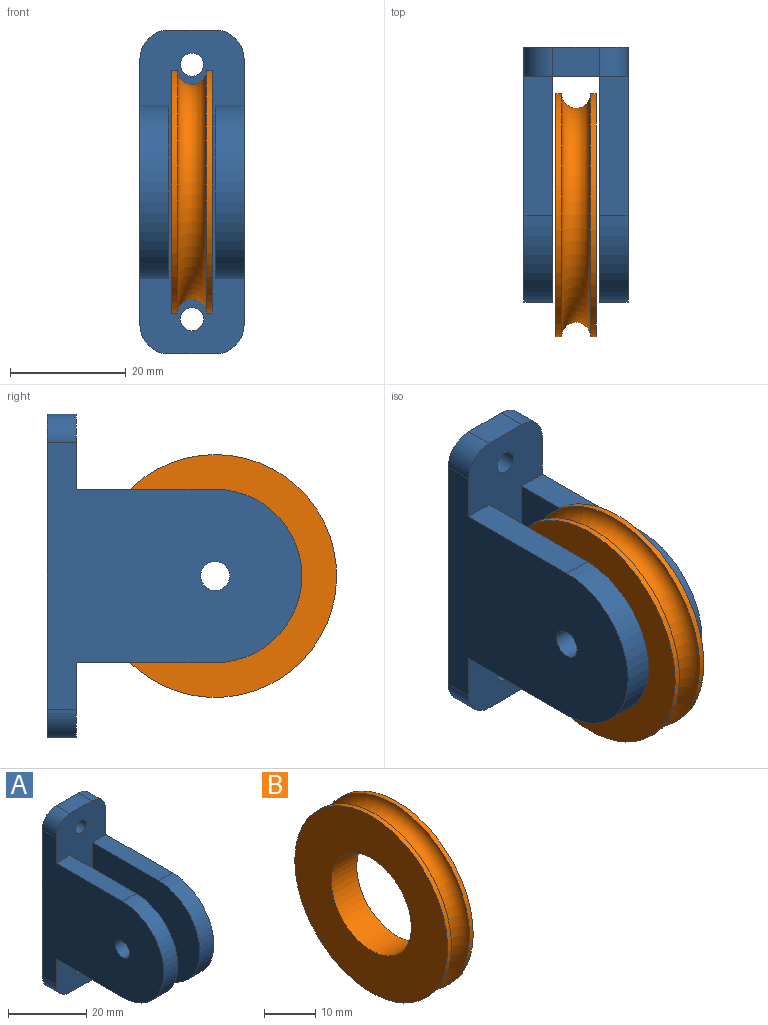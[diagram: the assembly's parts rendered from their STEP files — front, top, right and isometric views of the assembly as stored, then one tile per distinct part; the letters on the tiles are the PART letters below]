
ASSEMBLY  parts=2 mates=1
PART A: 22 faces, bbox 18x44x56 mm
  f0: cylinder r=15mm len=30mm, axis (1,0,0), area 235.6mm2, adj f1,f3,f4,f5
  f1: plane 24x5mm, normal (0,0,-1), area 120mm2, adj f0,f4,f5,f6
  f2: cylinder r=2.5mm len=5mm, axis (1,0,0), area 78.5mm2, adj f4,f5
  f3: plane 24x5mm, normal (0,0,1), area 120mm2, adj f0,f4,f5,f6
  f4: plane 39x30mm, normal (-1,0,0), area 1053.8mm2, adj f0,f1,f2,f3,f6
  f5: plane 46x44mm, normal (1,0,0), area 1283.8mm2, adj f0,f1,f2,f3,f6,f12,f19,f20
  f6: plane 56x18mm, normal (0,-1,0), area 661.4mm2, adj f1,f3,f4,f5,f7,f8,f9,f10
  f7: plane 46x44mm, normal (-1,0,0), area 1283.8mm2, adj f6,f12,f13,f14,f15,f16,f18,f21
  f8: plane 8x5mm, normal (0,0,-1), area 40mm2, adj f6,f12,f18,f19
  f9: cylinder r=2mm len=5mm, axis (0,1,0), area 62.8mm2, adj f6,f12
  f10: plane 8x5mm, normal (0,0,1), area 40mm2, adj f6,f12,f20,f21
  f11: cylinder r=2mm len=5mm, axis (0,1,0), area 62.8mm2, adj f6,f12
  f12: plane 56x18mm, normal (0,1,0), area 961.4mm2, adj f5,f7,f8,f9,f10,f11,f18,f19
  f13: cylinder r=15mm len=30mm, axis (1,0,0), area 235.6mm2, adj f7,f14,f16,f17
  f14: plane 24x5mm, normal (0,0,-1), area 120mm2, adj f6,f7,f13,f17
  f15: cylinder r=2.5mm len=5mm, axis (1,0,0), area 78.5mm2, adj f7,f17
  f16: plane 24x5mm, normal (0,0,1), area 120mm2, adj f6,f7,f13,f17
  f17: plane 39x30mm, normal (1,0,0), area 1053.8mm2, adj f6,f13,f14,f15,f16
  f18: cylinder r=5mm len=5mm, axis (0,-1,0), area 39.3mm2, adj f6,f7,f8,f12
  f19: cylinder r=5mm len=5mm, axis (0,-1,0), area 39.3mm2, adj f5,f6,f8,f12
  f20: cylinder r=5mm len=5mm, axis (0,1,0), area 39.3mm2, adj f5,f6,f10,f12
  f21: cylinder r=5mm len=5mm, axis (0,1,0), area 39.3mm2, adj f6,f7,f10,f12
PART B: 6 faces, bbox 7x49.3x49.3 mm
  f0: plane 42x42mm, normal (-1,0,0), area 1005.3mm2, adj f1,f5
  f1: cylinder r=11mm len=22mm, axis (-1,0,0), area 483.8mm2, adj f0,f2
  f2: plane 42x42mm, normal (1,0,0), area 1005.3mm2, adj f1,f3
  f3: cylinder r=21mm len=42mm, axis (-1,0,0), area 134.9mm2, adj f2,f4
  f4: torus R=21mm, axis (-1,0,0), area 949.9mm2, adj f3,f5
  f5: cylinder r=21mm len=42mm, axis (-1,0,0), area 134.9mm2, adj f0,f4
PLACE A t=(-23.54,-23.87,-21.82)mm
PLACE B t=(-3.04,-23.87,-21.82)mm
MATE revolute B.f1 <-> A.f2  axis (-1,0,0) through (-3.04,-23.87,-21.82)mm
